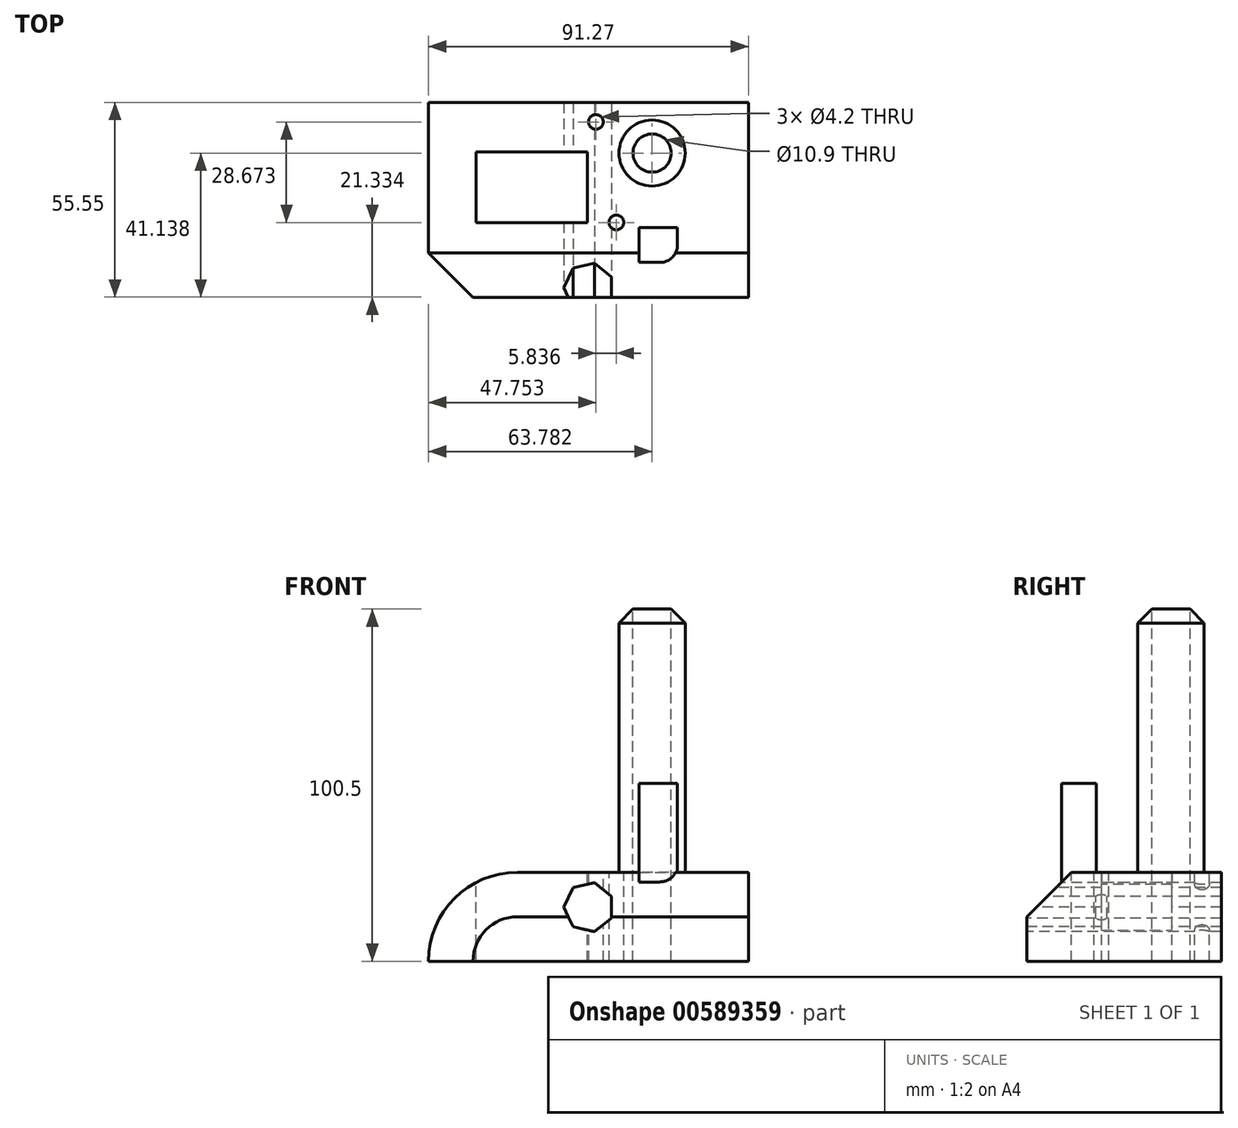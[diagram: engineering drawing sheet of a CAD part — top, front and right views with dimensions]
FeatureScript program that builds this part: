
annotation { "Feature Type Name" : "Feature", "Feature Type Description" : "" }
export const myFeature = defineFeature(function(context is Context, id is Id, definition is map)
    precondition{}
    {
        {
            var Q0;
            Q0=qCreatedBy(makeId("Top.planeOp"),FACE);
            var sketch = newSketch(context, id + "F0", { "sketchPlane" : qUnion([Q0])});
            skLineSegment(sketch, "E0.bottom", {"start": v(-91.27, -55.55) * mm, "end": v(0, -55.55) * mm});
            skLineSegment(sketch, "E0.top", {"start": v(-91.27, 0) * mm, "end": v(0, 0) * mm});
            skLineSegment(sketch, "E0.left", {"start": v(-91.27, -55.55) * mm, "end": v(-91.27, 0) * mm});
            skLineSegment(sketch, "E0.right", {"start": v(0, -55.55) * mm, "end": v(0, 0) * mm});
            skSolve(sketch);
        }
        {
            var Q0;
            Q0=makeQuery(id+"F0.imprint","IMPRINT",FACE,{"disambiguationData":[TD([[makeQuery(id+"F0.imprint","IMPRINT",EDGE,{"derivedFrom":sQuery(id+"F0.wireOp",EDGE,"E0.bottom")}),1.0]])]});
            extrude(context, id + "F1", {"entities" : qUnion([Q0]), "depth" : 25.4 * mm, "offsetDistance" : 25.4 * mm});
        }
        {
            var Q0;
            Q0=makeQuery(id+"F1.opExtrude","CAP_FACE",FACE,{"disambiguationData":[OSD([sQuery(id+"F0.wireOp",EDGE,"E0.bottom"),sQuery(id+"F0.wireOp",EDGE,"E0.top"),sQuery(id+"F0.wireOp",EDGE,"E0.left"),sQuery(id+"F0.wireOp",EDGE,"E0.right")])],"isStart":false});
            var sketch = newSketch(context, id + "F2", { "sketchPlane" : qUnion([Q0])});
            skLineSegment(sketch, "E1.bottom", {"start": v(-77.65, -14.1) * mm, "end": v(-45.94, -14.1) * mm});
            skLineSegment(sketch, "E1.top", {"start": v(-77.65, -34.22) * mm, "end": v(-45.94, -34.22) * mm});
            skLineSegment(sketch, "E1.left", {"start": v(-77.65, -14.1) * mm, "end": v(-77.65, -34.22) * mm});
            skLineSegment(sketch, "E1.right", {"start": v(-45.94, -14.1) * mm, "end": v(-45.94, -34.22) * mm});
            skSolve(sketch);
        }
        {
            var Q0;
            Q0=makeQuery(id+"F2.imprint","IMPRINT",FACE,{"disambiguationData":[TD([[makeQuery(id+"F2.imprint","IMPRINT",EDGE,{"derivedFrom":sQuery(id+"F2.wireOp",EDGE,"E1.bottom")}),-1.0]])]});
            extrude(context, id + "F3", {"entities" : qUnion([Q0]), "operationType" : NewBodyOperationType.REMOVE, "endBound" : BoundingType.THROUGH_ALL, "oppositeDirection" : true, "depth" : 33.27 * mm, "offsetDistance" : 25.4 * mm});
        }
        {
            var Q0;
            Q0=makeQuery(id+"F1.opExtrude","CAP_FACE",FACE,{"disambiguationData":[OSD([sQuery(id+"F0.wireOp",EDGE,"E0.bottom"),sQuery(id+"F0.wireOp",EDGE,"E0.top"),sQuery(id+"F0.wireOp",EDGE,"E0.left"),sQuery(id+"F0.wireOp",EDGE,"E0.right")])],"isStart":false});
            var sketch = newSketch(context, id + "F4", { "sketchPlane" : qUnion([Q0])});
            skCircle(sketch, "E2", {"center": v(-27.49, -14.41) * mm, "radius": 9.43 * mm});
            skSolve(sketch);
        }
        {
            var Q0;
            Q0=makeQuery(id+"F4.imprint","IMPRINT",FACE,{"disambiguationData":[TD([[makeQuery(id+"F4.imprint","IMPRINT",EDGE,{"derivedFrom":sQuery(id+"F4.wireOp",EDGE,"E2")}),1.0]])]});
            extrude(context, id + "F5", {"entities" : qUnion([Q0]), "operationType" : NewBodyOperationType.ADD, "depth" : 76.2 * mm, "offsetDistance" : 25.4 * mm});
        }
        {
            var Q0;
            Q0=makeQuery(id+"F1.opExtrude","SWEPT_FACE",FACE,{"disambiguationData":[OSD([sQuery(id+"F0.wireOp",EDGE,"E0.bottom")])]});
            var sketch = newSketch(context, id + "F6", { "sketchPlane" : qUnion([Q0])});
            skCircle(sketch, "E3.cCircle", {"center": v(-45.54, 15.41) * mm, "radius": 6.46 * mm, "construction": true});
            skLineSegment(sketch, "E3.0", {"start": v(-39.08, 18.52) * mm, "end": v(-39.08, 12.3) * mm});
            skLineSegment(sketch, "E3.1", {"start": v(-39.08, 12.3) * mm, "end": v(-43.95, 8.42) * mm});
            skLineSegment(sketch, "E3.2", {"start": v(-43.95, 8.42) * mm, "end": v(-50.01, 9.8) * mm});
            skLineSegment(sketch, "E3.3", {"start": v(-50.01, 9.8) * mm, "end": v(-52.72, 15.41) * mm});
            skLineSegment(sketch, "E3.4", {"start": v(-52.72, 15.41) * mm, "end": v(-50.01, 21.02) * mm});
            skLineSegment(sketch, "E3.5", {"start": v(-50.01, 21.02) * mm, "end": v(-43.95, 22.4) * mm});
            skLineSegment(sketch, "E3.6", {"start": v(-43.95, 22.4) * mm, "end": v(-39.08, 18.52) * mm});
            skPoint(sketch, "E3.0.midPoint", {"position": v(-39.08, 15.41) * mm});
            skSolve(sketch);
        }
        {
            var Q0;
            Q0=makeQuery(id+"F6.imprint","IMPRINT",FACE,{"disambiguationData":[TD([[makeQuery(id+"F6.imprint","IMPRINT",EDGE,{"derivedFrom":sQuery(id+"F6.wireOp",EDGE,"E3.0")}),-1.0]])]});
            extrude(context, id + "F7", {"entities" : qUnion([Q0]), "operationType" : NewBodyOperationType.REMOVE, "endBound" : BoundingType.THROUGH_ALL, "oppositeDirection" : true, "depth" : 25.4 * mm, "offsetDistance" : 25.4 * mm});
        }
        {
            var Q0;
            Q0=makeQuery(id+"F5.opExtrude","CAP_FACE",FACE,{"disambiguationData":[OSD([sQuery(id+"F4.wireOp",EDGE,"E2")])],"isStart":false});
            var sketch = newSketch(context, id + "F8", { "sketchPlane" : qUnion([Q0])});
            skCircle(sketch, "E4", {"center": v(-27.49, -14.41) * mm, "radius": 5.45 * mm});
            skSolve(sketch);
        }
        {
            var Q0;
            Q0=makeQuery(id+"F8.imprint","IMPRINT",FACE,{"disambiguationData":[TD([[makeQuery(id+"F8.imprint","IMPRINT",EDGE,{"derivedFrom":sQuery(id+"F8.wireOp",EDGE,"E4")}),1.0]])]});
            extrude(context, id + "F9", {"entities" : qUnion([Q0]), "operationType" : NewBodyOperationType.REMOVE, "endBound" : BoundingType.THROUGH_ALL, "oppositeDirection" : true, "depth" : 25.4 * mm, "offsetDistance" : 25.4 * mm});
        }
        {
            var Q0;
            Q0=makeQuery(id+"F1.opExtrude","CAP_FACE",FACE,{"disambiguationData":[OSD([sQuery(id+"F0.wireOp",EDGE,"E0.bottom"),sQuery(id+"F0.wireOp",EDGE,"E0.top"),sQuery(id+"F0.wireOp",EDGE,"E0.left"),sQuery(id+"F0.wireOp",EDGE,"E0.right")])],"isStart":false});
            var sketch = newSketch(context, id + "F10", { "sketchPlane" : qUnion([Q0])});
            skLineSegment(sketch, "E5.bottom", {"start": v(-31.2, -35.67) * mm, "end": v(-20.23, -35.67) * mm});
            skLineSegment(sketch, "E5.top", {"start": v(-31.2, -45.63) * mm, "end": v(-20.23, -45.63) * mm});
            skLineSegment(sketch, "E5.left", {"start": v(-31.2, -35.67) * mm, "end": v(-31.2, -45.63) * mm});
            skLineSegment(sketch, "E5.right", {"start": v(-20.23, -35.67) * mm, "end": v(-20.23, -45.63) * mm});
            skSolve(sketch);
        }
        {
            var Q0;
            Q0=makeQuery(id+"F10.imprint","IMPRINT",FACE,{"disambiguationData":[TD([[makeQuery(id+"F10.imprint","IMPRINT",EDGE,{"derivedFrom":sQuery(id+"F10.wireOp",EDGE,"E5.bottom")}),-1.0]])]});
            extrude(context, id + "F11", {"entities" : qUnion([Q0]), "operationType" : NewBodyOperationType.ADD, "depth" : 25.4 * mm, "offsetDistance" : 25.4 * mm});
        }
        {
            var Q0;
            Q0=makeQuery(id+"F1.opExtrude","CAP_EDGE",EDGE,{"disambiguationData":[OSD([sQuery(id+"F0.wireOp",EDGE,"E0.left")])],"isStart":false});
            fillet(context, id + "F12", {"entities" : qUnion([Q0]), "radius" : 25.4 * mm, "tangentPropagation" : true, "allowEdgeOverflow" : false});
        }
        {
            var Q0;
            Q0=makeQuery(id+"F1.opExtrude","CAP_EDGE",EDGE,{"disambiguationData":[OSD([sQuery(id+"F0.wireOp",EDGE,"E0.bottom")])],"isStart":false});
            chamfer(context, id + "F13", {"entities" : qUnion([Q0]), "width" : 12.7 * mm, "tangentPropagation" : true});
        }
        {
            var Q0;
            Q0=makeQuery(id+"F5.opExtrude","CAP_EDGE",EDGE,{"disambiguationData":[OSD([sQuery(id+"F4.wireOp",EDGE,"E2")])],"isStart":false});
            chamfer(context, id + "F14", {"entities" : qUnion([Q0]), "width" : 5.08 * mm, "tangentPropagation" : true});
        }
        {
            var Q0;
            Q0=makeQuery(id+"F11.opExtrude","SWEPT_EDGE",EDGE,{"disambiguationData":[OSD([sQuery(id+"F10.wireOp",EDGE,"E5.top"),sQuery(id+"F10.wireOp",EDGE,"E5.right")])]});
            fillet(context, id + "F15", {"entities" : qUnion([Q0]), "radius" : 5.08 * mm, "tangentPropagation" : true, "allowEdgeOverflow" : false});
        }
        {
            var Q0;
            Q0=makeQuery(id+"F1.opExtrude","CAP_FACE",FACE,{"disambiguationData":[OSD([sQuery(id+"F0.wireOp",EDGE,"E0.bottom"),sQuery(id+"F0.wireOp",EDGE,"E0.top"),sQuery(id+"F0.wireOp",EDGE,"E0.left"),sQuery(id+"F0.wireOp",EDGE,"E0.right")])],"isStart":false});
            var sketch = newSketch(context, id + "F16", { "sketchPlane" : qUnion([Q0])});
            skPoint(sketch, "E6", {"position": v(-37.68, -34.22) * mm});
            skPoint(sketch, "E7", {"position": v(-43.52, -5.54) * mm});
            skSolve(sketch);
        }
        {
            var Q0;
            Q0=sQuery(id+"F16.wireOp",VERTEX,"E6");
            var Q1;
            Q1=sQuery(id+"F16.wireOp",VERTEX,"E7");
            var Q2;
            Q2=makeQuery(id+"F1.opExtrude","SWEPT_BODY",BODY,{"disambiguationData":[OSD([sQuery(id+"F0.wireOp",EDGE,"E0.bottom"),sQuery(id+"F0.wireOp",EDGE,"E0.top"),sQuery(id+"F0.wireOp",EDGE,"E0.left"),sQuery(id+"F0.wireOp",EDGE,"E0.right")])]});
            hole(context, id + "F17", {"style" : HoleStyle.SIMPLE, "endStyle" : HoleEndStyle.THROUGH, "standardTappedOrClearance" : lookupTablePath({ "standard" : "ISO", "engagement" : "75%", "pitch" : "0.8 mm", "size" : "M5", "type" : "Tapped" }), "standardBlindInLast" : lookupTablePath({ "standard" : "ISO", "engagement" : "75%", "pitch" : "0.8 mm", "size" : "M5", "type" : "Tapped" }), "holeDiameter" : 4.2 * mm, "majorDiameter" : 5 * mm, "showTappedDepth" : true, "isTappedThrough" : true, "tappedDepth" : 12.7 * mm, "tapClearance" : 3, "locations" : qUnion([Q0, Q1]), "scope" : qUnion([Q2])});
        }
        {
            var Q0;
            Q0=makeQuery(id+"F12.opFillet","BLEND_EDGE",EDGE,{"blendedFrom":[makeQuery(id+"F1.opExtrude","CAP_EDGE",EDGE,{"disambiguationData":[OSD([sQuery(id+"F0.wireOp",EDGE,"E0.left")])],"isStart":false}),makeQuery(id+"F1.opExtrude","SWEPT_FACE",FACE,{"disambiguationData":[OSD([sQuery(id+"F0.wireOp",EDGE,"E0.top")])]})],"blendedInto":[makeQuery(id+"F1.opExtrude","SWEPT_FACE",FACE,{"disambiguationData":[OSD([sQuery(id+"F0.wireOp",EDGE,"E0.top")])]})]});
            fillet(context, id + "F18", {"entities" : qUnion([Q0]), "radius" : 0.25 * mm, "tangentPropagation" : true, "allowEdgeOverflow" : false});
        }
    });
